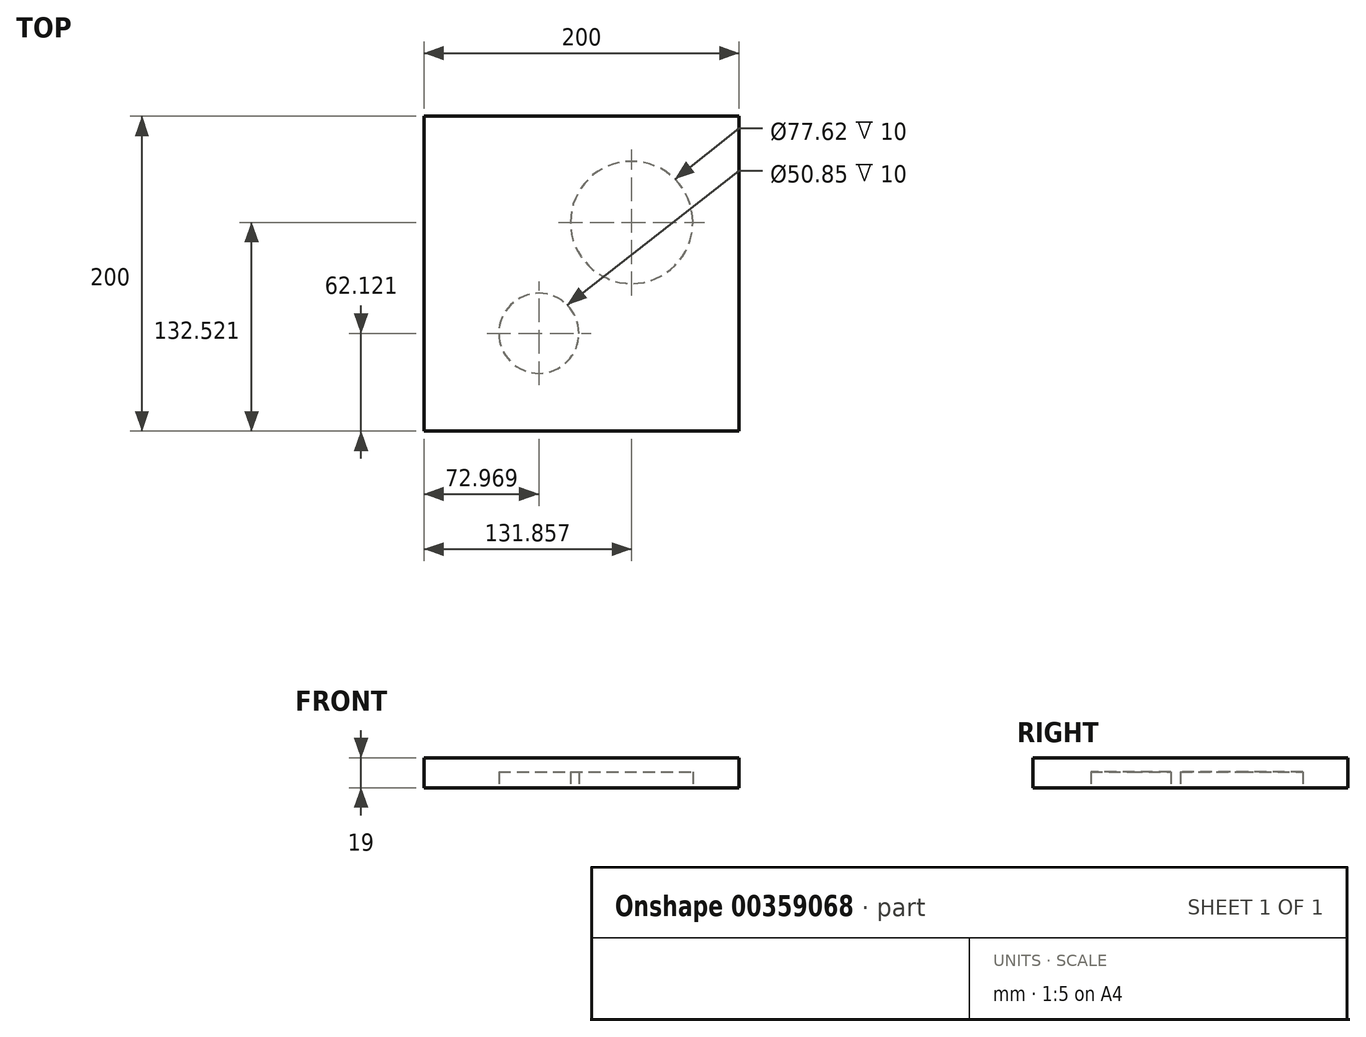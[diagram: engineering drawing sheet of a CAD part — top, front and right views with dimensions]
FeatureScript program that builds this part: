
annotation { "Feature Type Name" : "Feature", "Feature Type Description" : "" }
export const myFeature = defineFeature(function(context is Context, id is Id, definition is map)
    precondition{}
    {
        {
            var Q0;
            Q0=qCreatedBy(makeId("Top.planeOp"),FACE);
            var sketch = newSketch(context, id + "F0", { "sketchPlane" : qUnion([Q0])});
            skLineSegment(sketch, "E0.bottom", {"start": v(0, 0) * mm, "end": v(200, 0) * mm});
            skLineSegment(sketch, "E0.top", {"start": v(0, 200) * mm, "end": v(200, 200) * mm});
            skLineSegment(sketch, "E0.left", {"start": v(0, 0) * mm, "end": v(0, 200) * mm});
            skLineSegment(sketch, "E0.right", {"start": v(200, 0) * mm, "end": v(200, 200) * mm});
            skCircle(sketch, "E1", {"center": v(37.54, 158.2) * mm, "radius": 24.69 * mm});
            skCircle(sketch, "E2", {"center": v(120.78, 101.53) * mm, "radius": 35.01 * mm});
            skCircle(sketch, "E3", {"center": v(45.07, 44.85) * mm, "radius": 35.26 * mm});
            skSolve(sketch);
        }
        {
            var Q0;
            Q0=makeQuery(id+"F0.imprint","IMPRINT",FACE,{"disambiguationData":[TD([[makeQuery(id+"F0.imprint","IMPRINT",EDGE,{"derivedFrom":sQuery(id+"F0.wireOp",EDGE,"E2")}),1.0]])]});
            var Q1;
            Q1=makeQuery(id+"F0.imprint","IMPRINT",FACE,{"disambiguationData":[TD([[makeQuery(id+"F0.imprint","IMPRINT",EDGE,{"derivedFrom":sQuery(id+"F0.wireOp",EDGE,"E0.bottom")}),1.0]])]});
            var Q2;
            Q2=makeQuery(id+"F0.imprint","IMPRINT",FACE,{"disambiguationData":[TD([[makeQuery(id+"F0.imprint","IMPRINT",EDGE,{"derivedFrom":sQuery(id+"F0.wireOp",EDGE,"E3")}),1.0]])]});
            var Q3;
            Q3=makeQuery(id+"F0.imprint","IMPRINT",FACE,{"disambiguationData":[TD([[makeQuery(id+"F0.imprint","IMPRINT",EDGE,{"derivedFrom":sQuery(id+"F0.wireOp",EDGE,"E1")}),1.0]])]});
            extrude(context, id + "F1", {"entities" : qUnion([Q0, Q1, Q2, Q3]), "depth" : 19 * mm});
        }
        {
            var Q0;
            Q0=makeQuery(id+"F1.opExtrude","CAP_FACE",FACE,{"disambiguationData":[OSD([sQuery(id+"F0.wireOp",EDGE,"E0.bottom"),sQuery(id+"F0.wireOp",EDGE,"E0.top"),sQuery(id+"F0.wireOp",EDGE,"E0.left"),sQuery(id+"F0.wireOp",EDGE,"E0.right")])],"isStart":true});
            var sketch = newSketch(context, id + "F2", { "sketchPlane" : qUnion([Q0])});
            skCircle(sketch, "E4", {"center": v(72.97, -62.12) * mm, "radius": 25.43 * mm});
            skCircle(sketch, "E5", {"center": v(131.86, -132.52) * mm, "radius": 38.81 * mm});
            skSolve(sketch);
        }
        {
            var Q0;
            Q0 = qSketchRegion(id + "F2", true);
            extrude(context, id + "F3", {"entities" : qUnion([Q0]), "operationType" : NewBodyOperationType.REMOVE, "oppositeDirection" : true, "depth" : 10 * mm});
        }
    });
